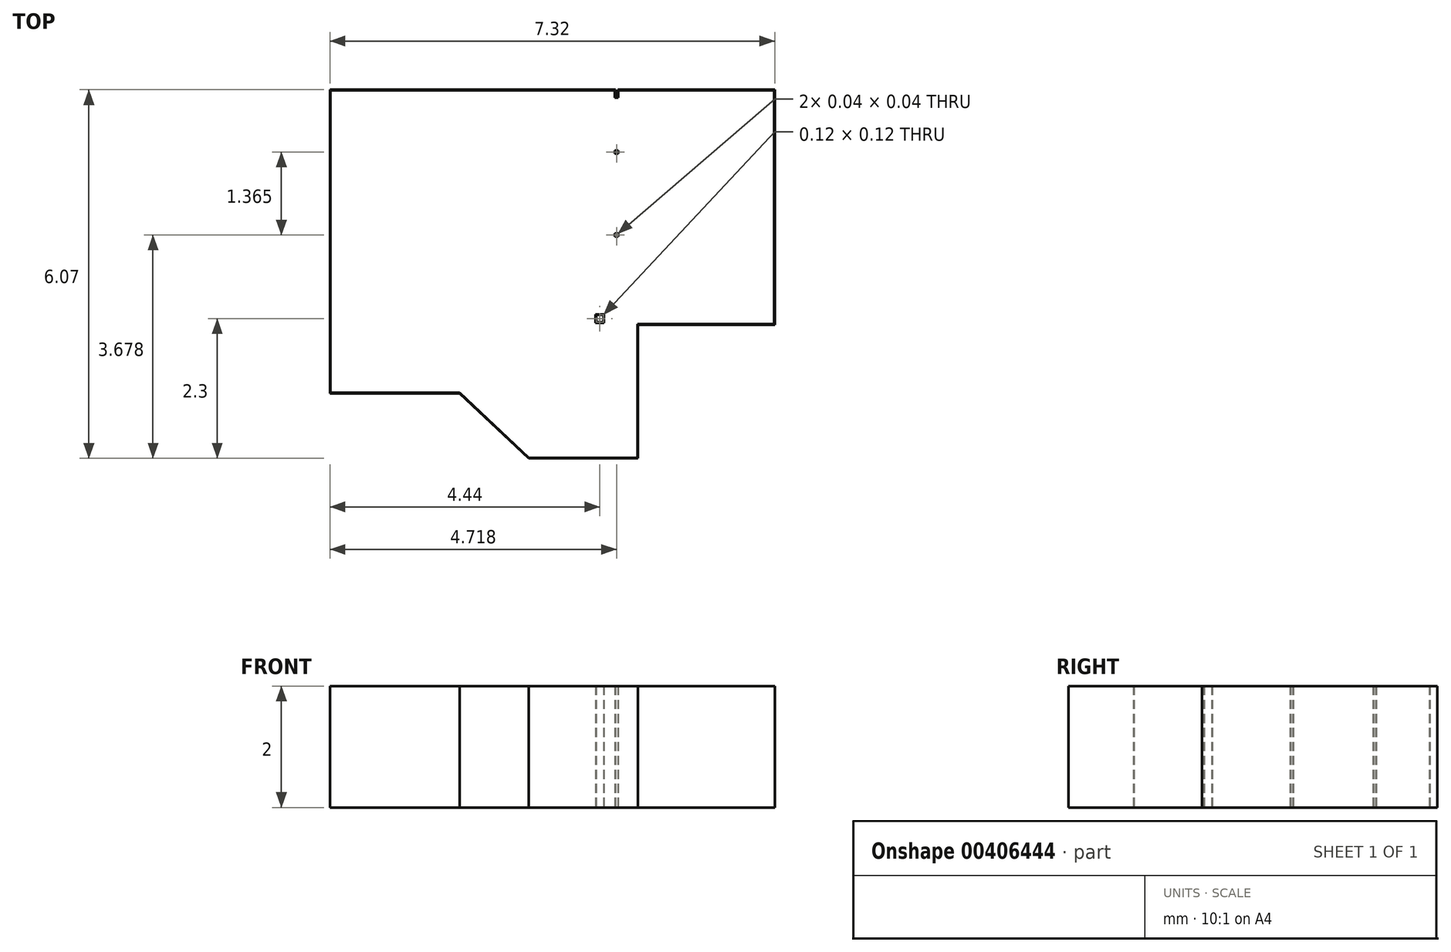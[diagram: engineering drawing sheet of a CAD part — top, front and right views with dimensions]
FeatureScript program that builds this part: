
annotation { "Feature Type Name" : "Feature", "Feature Type Description" : "" }
export const myFeature = defineFeature(function(context is Context, id is Id, definition is map)
    precondition{}
    {
        {
            var Q0;
            Q0=qCreatedBy(makeId("Top.planeOp"),FACE);
            var sketch = newSketch(context, id + "F0", { "sketchPlane" : qUnion([Q0])});
            skLineSegment(sketch, "E0.left", {"start": v(0, 0) * mm, "end": v(0, 5) * mm});
            skLineSegment(sketch, "E1.right", {"start": v(7.32, 5) * mm, "end": v(7.32, 1.13) * mm});
            skLineSegment(sketch, "E2", {"start": v(4.7, 5) * mm, "end": v(4.7, 4.88) * mm});
            skLineSegment(sketch, "E3", {"start": v(4.7, 4) * mm, "end": v(4.7, 3.96) * mm});
            skLineSegment(sketch, "E4", {"start": v(4.7, 2.62) * mm, "end": v(4.7, 2.6) * mm});
            skLineSegment(sketch, "E5", {"start": v(4.7, 2.6) * mm, "end": v(4.73, 2.6) * mm});
            skLineSegment(sketch, "E6", {"start": v(4.73, 2.6) * mm, "end": v(4.73, 2.62) * mm});
            skLineSegment(sketch, "E7", {"start": v(4.7, 2.62) * mm, "end": v(4.73, 2.62) * mm});
            skLineSegment(sketch, "E8", {"start": v(4.7, 4) * mm, "end": v(4.73, 4) * mm});
            skLineSegment(sketch, "E9", {"start": v(4.73, 4) * mm, "end": v(4.73, 3.96) * mm});
            skLineSegment(sketch, "E10", {"start": v(4.73, 3.96) * mm, "end": v(4.7, 3.96) * mm});
            skLineSegment(sketch, "E11", {"start": v(4.7, 4.88) * mm, "end": v(4.73, 4.88) * mm});
            skLineSegment(sketch, "E12", {"start": v(4.73, 4.88) * mm, "end": v(4.73, 5) * mm});
            skLineSegment(sketch, "E13", {"start": v(7.32, 1.13) * mm, "end": v(5.07, 1.13) * mm});
            skLineSegment(sketch, "E14", {"start": v(5.07, 1.13) * mm, "end": v(5.07, -1.07) * mm});
            skLineSegment(sketch, "E15", {"start": v(5.07, -1.07) * mm, "end": v(3.27, -1.07) * mm});
            skLineSegment(sketch, "E16", {"start": v(0, 0) * mm, "end": v(2.13, 0) * mm});
            skLineSegment(sketch, "E17", {"start": v(0, 5) * mm, "end": v(7.32, 5) * mm});
            skLineSegment(sketch, "E18", {"start": v(2.13, 0) * mm, "end": v(3.27, -1.07) * mm});
            skLineSegment(sketch, "E19", {"start": v(4.5, 1.17) * mm, "end": v(4.5, 1.29) * mm});
            skLineSegment(sketch, "E20", {"start": v(4.5, 1.29) * mm, "end": v(4.38, 1.29) * mm});
            skLineSegment(sketch, "E21", {"start": v(4.38, 1.29) * mm, "end": v(4.38, 1.17) * mm});
            skLineSegment(sketch, "E22", {"start": v(4.38, 1.17) * mm, "end": v(4.5, 1.17) * mm});
            skSolve(sketch);
        }
        {
            var Q0;
            {var subQ1=sQuery(id+"F0.wireOp",EDGE,"E0.left");Q0=makeQuery(id+"F0.imprint","IMPRINT",FACE,{"disambiguationData":[TD([[makeQuery(id+"F0.imprint","IMPRINT",EDGE,{"derivedFrom":subQ1}),-1.0]])]});}
            extrude(context, id + "F1", {"entities" : qUnion([Q0]), "depth" : 2 * mm});
        }
        {
            var Q0;
            Q0=makeQuery(id+"F1.opExtrude","CAP_FACE",FACE,{"disambiguationData":[OSD([sQuery(id+"F0.wireOp",EDGE,"E0.left"),sQuery(id+"F0.wireOp",EDGE,"E1.right"),sQuery(id+"F0.wireOp",EDGE,"E2"),sQuery(id+"F0.wireOp",EDGE,"E3"),sQuery(id+"F0.wireOp",EDGE,"E4"),sQuery(id+"F0.wireOp",EDGE,"AGYnJl51-9QUN-N7XJ-JuIY-aywVxIPcn9cS"),sQuery(id+"F0.wireOp",EDGE,"E5"),sQuery(id+"F0.wireOp",EDGE,"E6"),sQuery(id+"F0.wireOp",EDGE,"E7"),sQuery(id+"F0.wireOp",EDGE,"E8"),sQuery(id+"F0.wireOp",EDGE,"E9"),sQuery(id+"F0.wireOp",EDGE,"E10"),sQuery(id+"F0.wireOp",EDGE,"E11"),sQuery(id+"F0.wireOp",EDGE,"E12"),sQuery(id+"F0.wireOp",EDGE,"aLozBtAa-tSo1-DUFU-ty26-sbqmOE57xnWO"),sQuery(id+"F0.wireOp",EDGE,"Qh6c7cnu-8fEK-zgRQ-zyQg-FWxUpxE0UMdV"),sQuery(id+"F0.wireOp",EDGE,"CDNCLsGT-dUBQ-HX5G-ICYw-cgrgQiEzy7Fy"),sQuery(id+"F0.wireOp",EDGE,"E13"),sQuery(id+"F0.wireOp",EDGE,"E14"),sQuery(id+"F0.wireOp",EDGE,"E15"),sQuery(id+"F0.wireOp",EDGE,"E16"),sQuery(id+"F0.wireOp",EDGE,"E17"),sQuery(id+"F0.wireOp",EDGE,"E18")])],"isStart":false});
            shell(context, id + "F2", {"entities" : qUnion([Q0]), "thickness" : 0.01 * mm});
        }
    });
